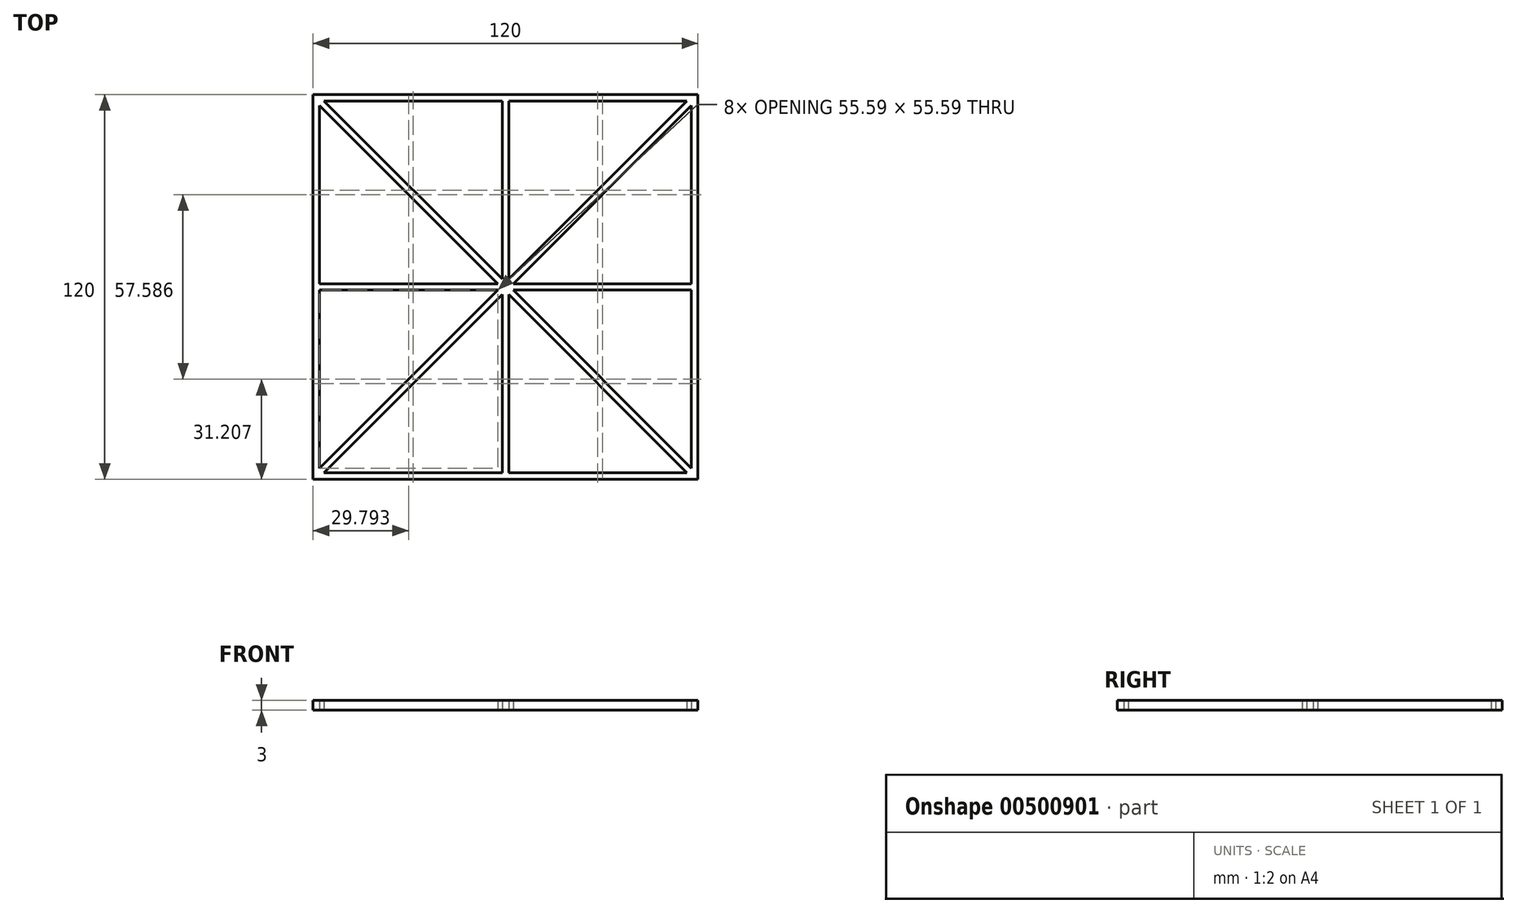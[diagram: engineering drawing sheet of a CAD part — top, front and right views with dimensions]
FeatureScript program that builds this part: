
annotation { "Feature Type Name" : "Feature", "Feature Type Description" : "" }
export const myFeature = defineFeature(function(context is Context, id is Id, definition is map)
    precondition{}
    {
        {
            var Q0;
            Q0=qCreatedBy(makeId("Top.planeOp"),FACE);
            var sketch = newSketch(context, id + "F0", { "sketchPlane" : qUnion([Q0])});
            skLineSegment(sketch, "E0.bottom", {"start": v(-60, 60) * mm, "end": v(60, 60) * mm});
            skLineSegment(sketch, "E0.top", {"start": v(-60, -60) * mm, "end": v(60, -60) * mm});
            skLineSegment(sketch, "E0.left", {"start": v(-60, 60) * mm, "end": v(-60, -60) * mm});
            skLineSegment(sketch, "E0.right", {"start": v(60, 60) * mm, "end": v(60, -60) * mm});
            skPoint(sketch, "E0.middle", {"position": v(0, 0) * mm});
            skLineSegment(sketch, "E1.0", {"start": v(-56.59, 58) * mm, "end": v(-1, 58) * mm});
            skLineSegment(sketch, "E1.1", {"start": v(-58, 56.59) * mm, "end": v(-58, 1) * mm});
            skLineSegment(sketch, "E1.2", {"start": v(-56.59, -58) * mm, "end": v(-1, -58) * mm});
            skLineSegment(sketch, "E1.3", {"start": v(58, 56.59) * mm, "end": v(58, 1) * mm});
            skLineSegment(sketch, "E2", {"start": v(-58, 0) * mm, "end": v(58, 0) * mm, "construction": true});
            skLineSegment(sketch, "E3", {"start": v(0, 58) * mm, "end": v(0, -58) * mm, "construction": true});
            skLineSegment(sketch, "E4.0", {"start": v(-1, 58) * mm, "end": v(-1, 2.41) * mm});
            skLineSegment(sketch, "E5.0", {"start": v(1, 58) * mm, "end": v(1, 2.41) * mm});
            skLineSegment(sketch, "E6.0", {"start": v(-58, -1) * mm, "end": v(-2.41, -1) * mm});
            skLineSegment(sketch, "E7.0", {"start": v(-58, 1) * mm, "end": v(-2.41, 1) * mm});
            skLineSegment(sketch, "E8.trimOffspring", {"start": v(1, -2.41) * mm, "end": v(1, -58) * mm});
            skLineSegment(sketch, "E9.trimOffspring", {"start": v(2.41, 1) * mm, "end": v(58, 1) * mm});
            skLineSegment(sketch, "E10.trimOffspring", {"start": v(-1, -2.41) * mm, "end": v(-1, -58) * mm});
            skLineSegment(sketch, "E11.trimOffspring", {"start": v(2.41, -1) * mm, "end": v(58, -1) * mm});
            skLineSegment(sketch, "E12", {"start": v(-60, 60) * mm, "end": v(58, -58) * mm, "construction": true});
            skLineSegment(sketch, "E13", {"start": v(58, 58) * mm, "end": v(-58, -58) * mm, "construction": true});
            skLineSegment(sketch, "E14.0", {"start": v(58, 56.59) * mm, "end": v(1.41, 0) * mm});
            skLineSegment(sketch, "E15.0", {"start": v(56.59, 58) * mm, "end": v(1, 2.41) * mm});
            skLineSegment(sketch, "E16.trimOffspring", {"start": v(-58, 56.59) * mm, "end": v(-2.41, 1) * mm});
            skLineSegment(sketch, "E17.trimOffspring", {"start": v(-56.59, 58) * mm, "end": v(58, -56.59) * mm});
            skPoint(sketch, "E18.orphan", {"position": v(-58, 58) * mm});
            skLineSegment(sketch, "E19.trimOffspring", {"start": v(-58, -1) * mm, "end": v(-58, -56.59) * mm});
            skLineSegment(sketch, "E20.trimOffspring", {"start": v(1, -58) * mm, "end": v(56.59, -58) * mm});
            skLineSegment(sketch, "E21.trimOffspring", {"start": v(58, -1) * mm, "end": v(58, -56.59) * mm});
            skLineSegment(sketch, "E22.trimOffspring", {"start": v(1, 58) * mm, "end": v(56.59, 58) * mm});
            skLineSegment(sketch, "E23.trimOffspring", {"start": v(-1, -2.41) * mm, "end": v(-56.59, -58) * mm});
            skLineSegment(sketch, "E24.trimOffspring", {"start": v(1, -2.41) * mm, "end": v(56.59, -58) * mm});
            skLineSegment(sketch, "E25.trimOffspring", {"start": v(-2.41, -1) * mm, "end": v(-58, -56.59) * mm});
            skLineSegment(sketch, "E26.trimOffspring", {"start": v(-1, 1) * mm, "end": v(-1, 0) * mm});
            skSolve(sketch);
        }
        {
            var Q0;
            Q0=makeQuery(id+"F0.imprint","IMPRINT",FACE,{"disambiguationData":[TD([[makeQuery(id+"F0.imprint","IMPRINT",EDGE,{"derivedFrom":sQuery(id+"F0.wireOp",EDGE,"E0.bottom")}),-1.0]])]});
            extrude(context, id + "F1", {"entities" : qUnion([Q0]), "depth" : 3 * mm});
        }
    });
